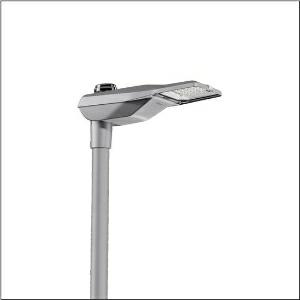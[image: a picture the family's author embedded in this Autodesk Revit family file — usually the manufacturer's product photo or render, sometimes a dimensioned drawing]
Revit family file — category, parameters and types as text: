
# Revit family: streetlight_sl_21_micro___st1_5a_5xe5p37n08db_dfc7
name_source: partatom
category: Lighting Fixtures
units: mm (PartAtom-declared; Revit-internal decimal feet)

## family parameters
Cut with Voids When Loaded = No
Host = Face
Light Source = No
Part Type = Normal
Room Calculation Point = No
Round Connector Dimension = Use Diameter
Shared = No

## types (1)
- --- (1 x LED, 5020 lm, 39.1 W, 3000K)
    Apparent Load = 39 VA
    CIE Flux Codes = 22 53 95 100 100
    Color Rendering = 70
    Color Temperature = 3000K
    Default Elevation = 1800 mm
    Description = Streetlight SL 21 micro, mast luminaire, primary light control with lens, of PMMA, primary optical cover: cover, of toughened safety glass, transparent, light distribution: ST1.5a, light emission: direct distribution, primary light characteristic: asymmetric, installation type: post-top, LED, 3G 1.5mm², High Power LED, rated luminous flux: 5.020lm, luminous efficacy: 128lm/W, light colour: 730, colour temperature: 3000K, control gear: NEMA (7pin), control: overheat protection, pre-setting: linear dimming characteristic, constant luminous flux control, time-dependent luminous flux control, flexible luminous flux parameterisation, mains connection: 230..240V, AC, 50/60Hz, connection cable pre-assembled, cable length: 6,5m, wiring characteristics: H07RN-F, start of lifetime: 39W, end of service life: 41W, reduction: 18W, luminaire housing, of diecast aluminium (EN AC-44300), powder-coated, Siteco® metallic grey (DB 702S), corrosivity category C5 mid according to DIN EN ISO 12944, multi-level sealing system, sealing non-destructively replaceable, inclination adjustable: 0°, 5°, 10°, 15°, length: 528mm, width: 235mm, height: 110mm, spigot size: 76/60mm (post-top), mounting height: 4..8m, protection rating (complete): IP66, insulation class (complete): insulation class I (protective earthing), certification: CE, ENEC, ENEC+, VDE, impact resistance: IK10, permissible operating ambient temperature for outdoor applications: -40..+50°C, standard-compliant lighting for roads and squares, packaging unit: 1 piece

Light Distribution: ST1.5a
    Height = 110 mm
    Lamp = 1 x LED
    Lamp Light Flux = 5020 lm
    Lamp Power = 39.1 W
    Lamp count = 1
    Length = 528 mm
    Luminous efficacy = 128 lm/W
    Manufacturer = Siteco
    ModVariant = No
    Model = 5XE5P37N08DB
    Number of Poles = 1
    OnlyDefault = Yes
    Power Factor = 1
    Product Name = Streetlight SL 21 micro | ST1.5a
    Product group = mast luminaire | pylon top
    ProductGroupID = 6100
    Protection Class = Protection class I
    Protection Degree = IP 66
    RLX_Detail_Level = 1
    RLX_Emergency_Light_Flux = 0 lm
    RLX_Emergency_Type = 0
    RLX_Emergency_Type_DB = No
    RlxData = <blob elided: 102389 chars, md5=b0bdf0b2>
    Socket = socket
    Standby Power = 0 W
    System Light Flux = 5020 lm
    System Power = 39 W
    Type Comments = factory setting: luminous flux: 100 % | dim-lin: 254 | 765 mA
    Type Image = l_1294375.jpg
    URL = http://relux.com
    VarID = @adj_155245
    Voltage = 0 V
    Weight = 0.00 kg
    Width = 235 mm

## geometry (parser evidence)
native form markers: Blend x4, Sweep x12
no freeform markers — native parametric forms only
